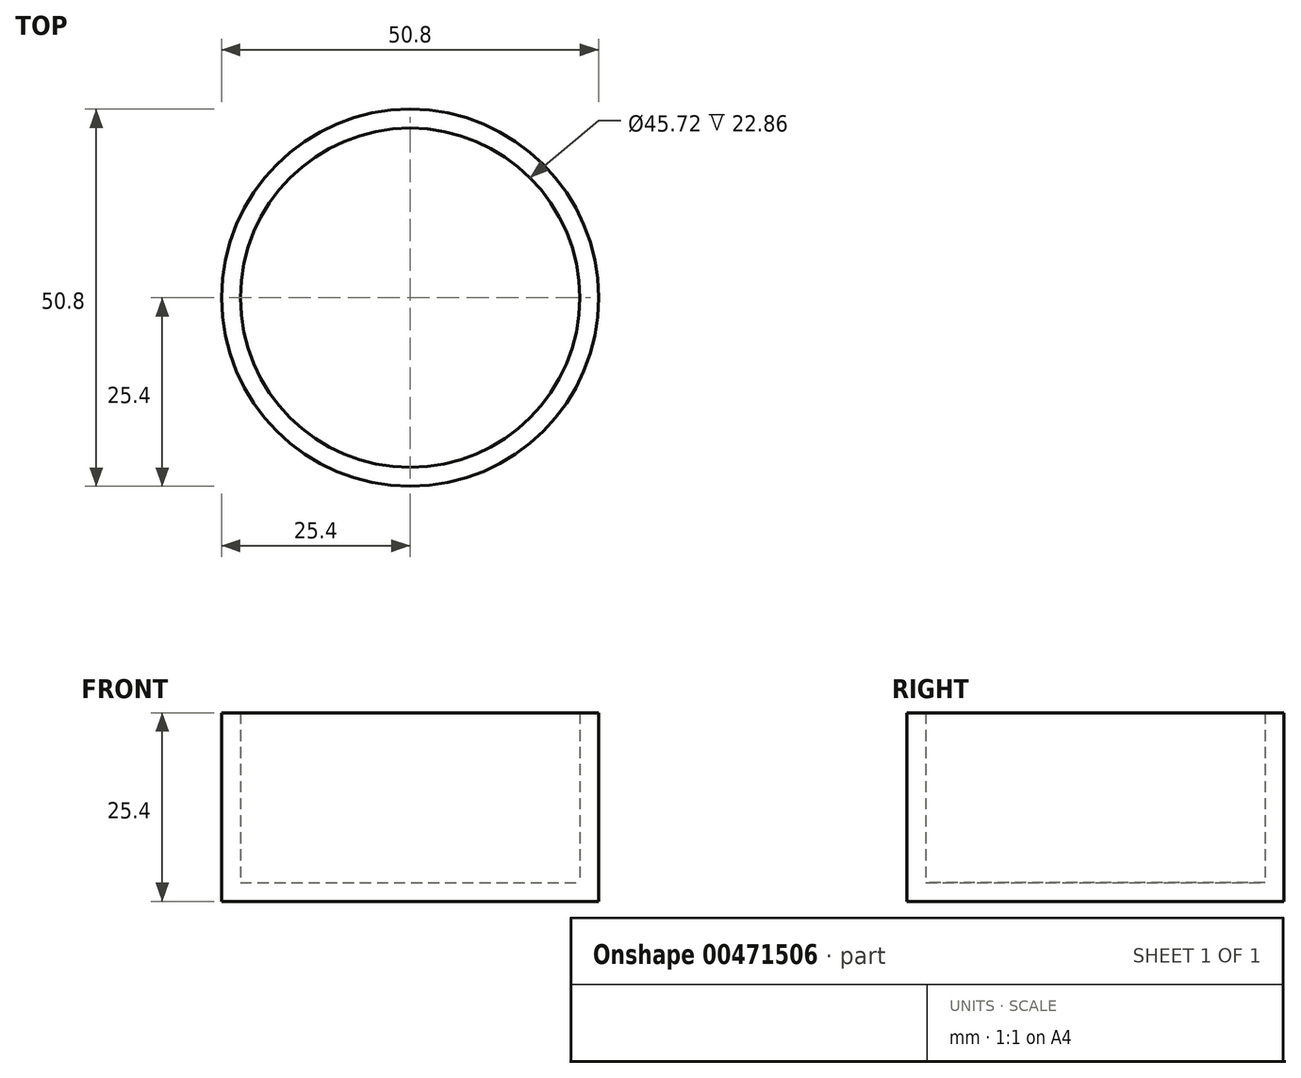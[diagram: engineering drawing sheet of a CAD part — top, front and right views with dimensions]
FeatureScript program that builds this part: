
annotation { "Feature Type Name" : "Feature", "Feature Type Description" : "" }
export const myFeature = defineFeature(function(context is Context, id is Id, definition is map)
    precondition{}
    {
        {
            var Q0;
            Q0=qCreatedBy(makeId("Front.planeOp"),FACE);
            var sketch = newSketch(context, id + "F0", { "sketchPlane" : qUnion([Q0])});
            skLineSegment(sketch, "E0.bottom", {"start": v(0, 0) * mm, "end": v(25.4, 0) * mm});
            skLineSegment(sketch, "E0.top", {"start": v(0, 25.4) * mm, "end": v(25.4, 25.4) * mm});
            skLineSegment(sketch, "E0.left", {"start": v(0, 0) * mm, "end": v(0, 25.4) * mm});
            skLineSegment(sketch, "E0.right", {"start": v(25.4, 0) * mm, "end": v(25.4, 25.4) * mm});
            skSolve(sketch);
        }
        {
            var Q0;
            Q0=makeQuery(id+"F0.imprint","IMPRINT",FACE,{"disambiguationData":[TD([[makeQuery(id+"F0.imprint","IMPRINT",EDGE,{"derivedFrom":sQuery(id+"F0.wireOp",EDGE,"E0.bottom")}),1.0]])]});
            var Q1;
            Q1=sQuery(id+"F0.wireOp",EDGE,"E0.left");
            revolve(context, id + "F1", {"entities" : qUnion([Q0]), "axis" : qUnion([Q1]), "revolveType" : RevolveType.FULL});
        }
        {
            var Q0;
            Q0=makeQuery(id+"F1.opRevolve","SWEPT_FACE",FACE,{"disambiguationData":[OSD([sQuery(id+"F0.wireOp",EDGE,"E0.top")])]});
            shell(context, id + "F2", {"entities" : qUnion([Q0]), "thickness" : 2.54 * mm});
        }
    });
